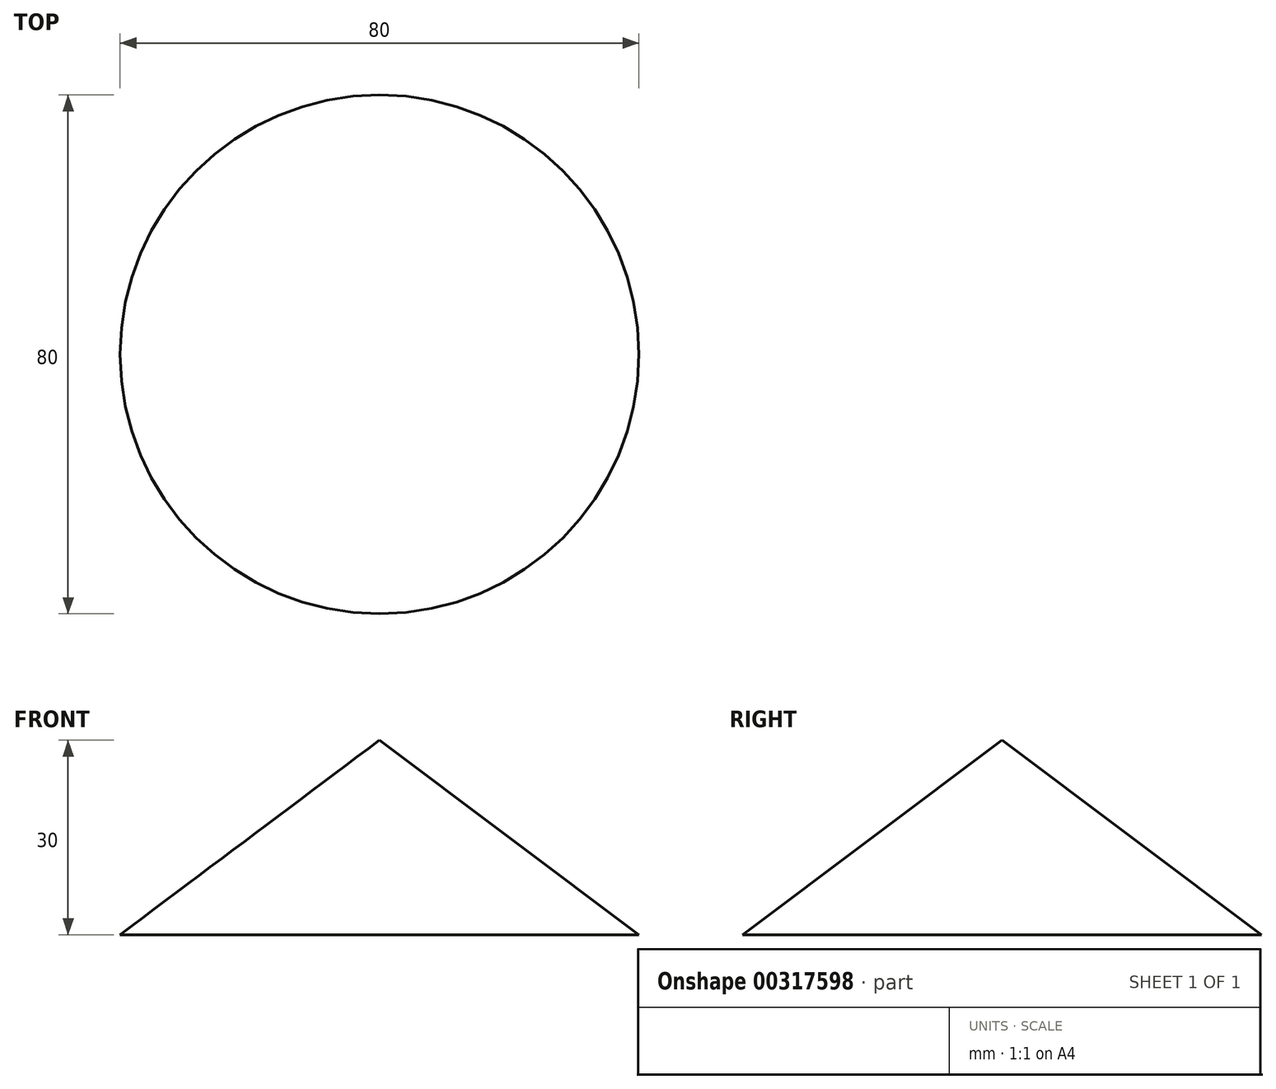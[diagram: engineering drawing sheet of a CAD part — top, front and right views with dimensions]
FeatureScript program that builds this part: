
annotation { "Feature Type Name" : "Feature", "Feature Type Description" : "" }
export const myFeature = defineFeature(function(context is Context, id is Id, definition is map)
    precondition{}
    {
        {
            var Q0;
            Q0=qCreatedBy(makeId("Front.planeOp"),FACE);
            var sketch = newSketch(context, id + "F0", { "sketchPlane" : qUnion([Q0])});
            skLineSegment(sketch, "E0", {"start": v(0, 0) * mm, "end": v(0, 30) * mm});
            skLineSegment(sketch, "E1", {"start": v(0, 30) * mm, "end": v(40, 0) * mm});
            skLineSegment(sketch, "E2", {"start": v(40, 0) * mm, "end": v(0, 0) * mm});
            skLineSegment(sketch, "E3", {"start": v(0, -78.5) * mm, "end": v(0, -108.5) * mm, "construction": true});
            skSolve(sketch);
        }
        {
            var Q0;
            Q0=makeQuery(id+"F0.imprint","IMPRINT",FACE,{"disambiguationData":[TD([[makeQuery(id+"F0.imprint","IMPRINT",EDGE,{"derivedFrom":sQuery(id+"F0.wireOp",EDGE,"E0")}),-1.0]])]});
            var Q1;
            Q1=sQuery(id+"F0.wireOp",EDGE,"E3");
            revolve(context, id + "F1", {"entities" : qUnion([Q0]), "axis" : qUnion([Q1]), "revolveType" : RevolveType.FULL});
        }
    });
